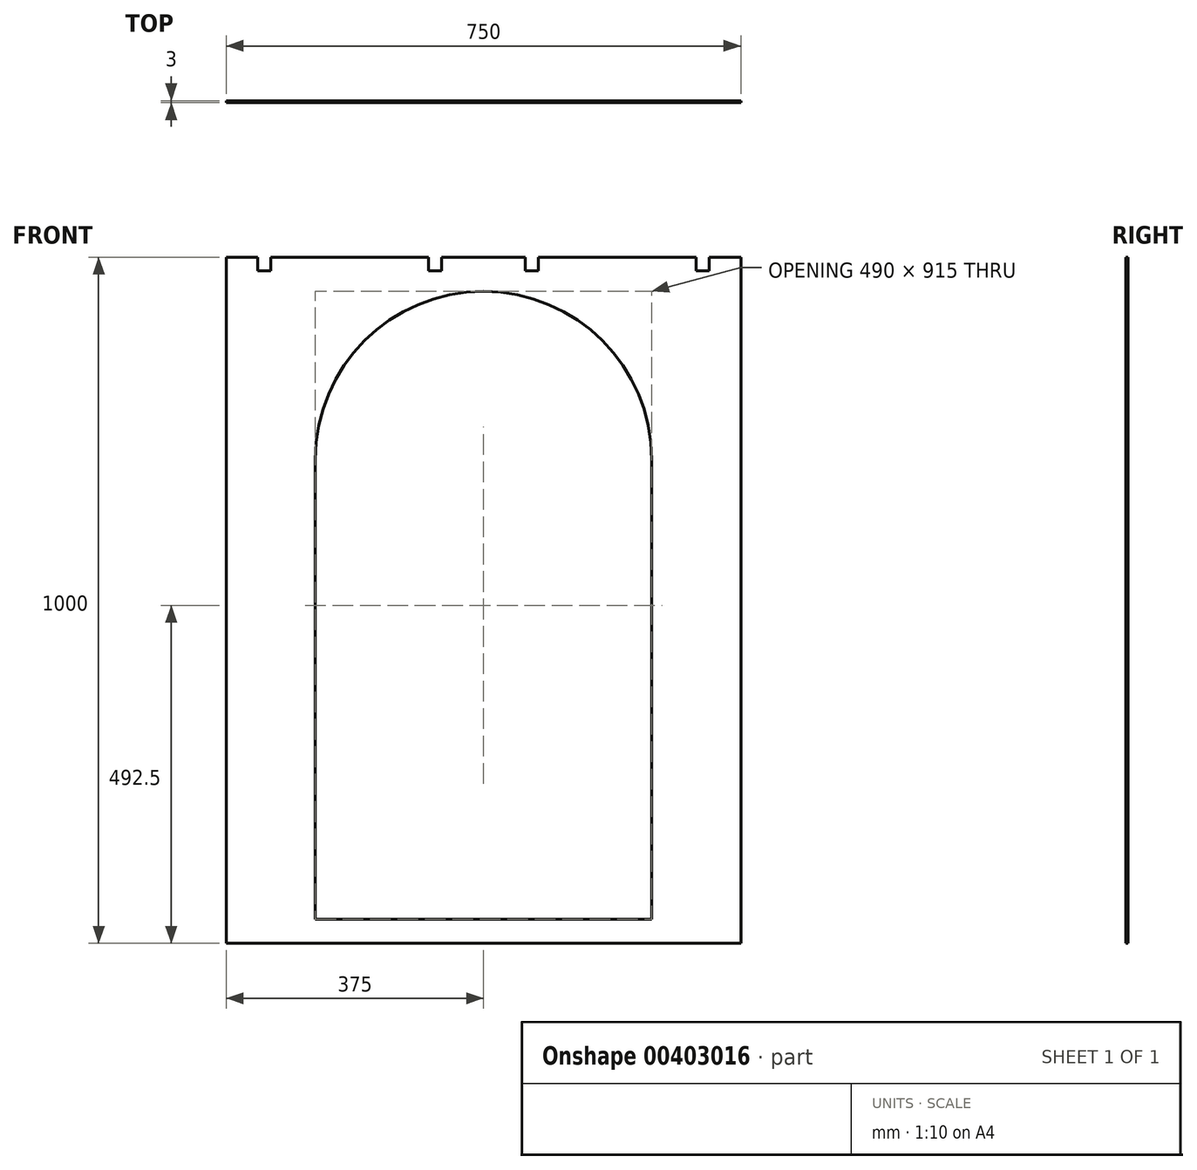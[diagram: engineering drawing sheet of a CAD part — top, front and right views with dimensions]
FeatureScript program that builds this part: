
annotation { "Feature Type Name" : "Feature", "Feature Type Description" : "" }
export const myFeature = defineFeature(function(context is Context, id is Id, definition is map)
    precondition{}
    {
        {
            var Q0;
            Q0=qCreatedBy(makeId("Front.planeOp"),FACE);
            var sketch = newSketch(context, id + "F0", { "sketchPlane" : qUnion([Q0])});
            skLineSegment(sketch, "E0.bottom", {"start": v(0, 0) * mm, "end": v(750, 0) * mm});
            skLineSegment(sketch, "E0.top", {"start": v(0, 1000) * mm, "end": v(46, 1000) * mm});
            skLineSegment(sketch, "E0.left", {"start": v(0, 0) * mm, "end": v(0, 1000) * mm});
            skLineSegment(sketch, "E0.right", {"start": v(750, 0) * mm, "end": v(750, 1000) * mm});
            skLineSegment(sketch, "E1.top", {"start": v(130, 35) * mm, "end": v(620, 35) * mm});
            skLineSegment(sketch, "E1.left", {"start": v(130, 705) * mm, "end": v(130, 35) * mm});
            skLineSegment(sketch, "E1.right", {"start": v(620, 705) * mm, "end": v(620, 35) * mm});
            skArc(sketch, "E2", {"start": v(620, 705) * mm, "mid": v(375, 950) * mm, "end": v(130, 705) * mm});
            skLineSegment(sketch, "E3.top", {"start": v(46, 980) * mm, "end": v(65, 980) * mm});
            skLineSegment(sketch, "E3.left", {"start": v(46, 1000) * mm, "end": v(46, 980) * mm});
            skLineSegment(sketch, "E3.right", {"start": v(65, 1000) * mm, "end": v(65, 980) * mm});
            skLineSegment(sketch, "E4.top", {"start": v(295, 980) * mm, "end": v(314, 980) * mm});
            skLineSegment(sketch, "E4.left", {"start": v(295, 1000) * mm, "end": v(295, 980) * mm});
            skLineSegment(sketch, "E4.right", {"start": v(314, 1000) * mm, "end": v(314, 980) * mm});
            skLineSegment(sketch, "E5.top", {"start": v(685, 980) * mm, "end": v(704, 980) * mm});
            skLineSegment(sketch, "E5.left", {"start": v(685, 1000) * mm, "end": v(685, 980) * mm});
            skLineSegment(sketch, "E5.right", {"start": v(704, 1000) * mm, "end": v(704, 980) * mm});
            skLineSegment(sketch, "E6.trimOffspring", {"start": v(65, 1000) * mm, "end": v(295, 1000) * mm});
            skLineSegment(sketch, "E7.trimOffspring", {"start": v(314, 1000) * mm, "end": v(436, 1000) * mm});
            skLineSegment(sketch, "E8.trimOffspring", {"start": v(704, 1000) * mm, "end": v(750, 1000) * mm});
            skLineSegment(sketch, "E9.top", {"start": v(436, 980) * mm, "end": v(455, 980) * mm});
            skLineSegment(sketch, "E9.left", {"start": v(436, 1000) * mm, "end": v(436, 980) * mm});
            skLineSegment(sketch, "E9.right", {"start": v(455, 1000) * mm, "end": v(455, 980) * mm});
            skLineSegment(sketch, "E10.trimOffspring", {"start": v(455, 1000) * mm, "end": v(685, 1000) * mm});
            skSolve(sketch);
        }
        {
            var Q0;
            Q0=makeQuery(id+"F0.imprint","IMPRINT",FACE,{"disambiguationData":[TD([[makeQuery(id+"F0.imprint","IMPRINT",EDGE,{"derivedFrom":sQuery(id+"F0.wireOp",EDGE,"E0.bottom")}),1.0]])]});
            extrude(context, id + "F1", {"entities" : qUnion([Q0]), "depth" : 3 * mm});
        }
    });
